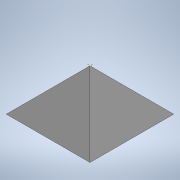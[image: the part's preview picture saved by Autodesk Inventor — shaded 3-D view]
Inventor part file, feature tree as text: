
AUTODESK INVENTOR PART (.ipt)
format: ipt  version: 2020 (Build 240168000, 168)  size: 123,904 bytes
history: native  units: in
note: dims shown in document units (in); Inventor stores cm internally (conversion verified against a paired STEP export)
features: sketch x6, extrude x5, plane x4
ambient origin geometry x8: Origin, YZ Plane, XZ Plane, XY Plane, X Axis, Y Axis, Z Axis, Center Point
bodies: Solid1 (feature_tree)
feature tree (15):
  extrude  "Extrusion1"  Depth=0.5906in
  sketch  "Sketch2"  dims[d2=0.2953in d3=0.0in]
  plane  "Work Plane1"
  plane  "Work Plane2"
  plane  "Work Plane3"
  plane  "Work Plane4"
  extrude  "Extrusion2"  TaperAngle=0.0deg  [1 undecoded]
  extrude  "Extrusion3"  Depth=0.1033in TaperAngle=0.0deg
  extrude  "Extrusion4"  TaperAngle=0.0deg  [1 undecoded]
  extrude  "Extrusion5"  [1 undecoded]
  sketch  "Sketch1"  dims[d0=0.5906in d1=0.5906in]
  sketch  "Sketch4"  dims[d4=0.1264in d5=0.0in d6=0.1033in d7=0.0in]
  sketch  "Sketch5"  dims[d8=0.5906in d9=0.0in]
  sketch  "Sketch6"  dims[d10=0.0508in d11=0.0in]
  sketch  "Sketch7"
note: 3 required parameter values undecoded (feature->parameter linkage not recoverable at this tier; creation-order binding heuristic only, values carry confidence <= 0.55)
